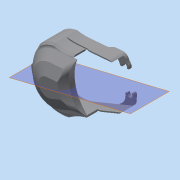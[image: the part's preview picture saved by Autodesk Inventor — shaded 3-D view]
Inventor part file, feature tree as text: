
AUTODESK INVENTOR PART (.ipt)
format: ipt  version: 2015 SP1 (Build 190203100, 203)  size: 975,360 bytes
history: native  units: in
note: dims shown in document units (in); Inventor stores cm internally (conversion verified against a paired STEP export)
features: extrude x14, fillet x14, sketch x14, chamfer x10, projected_geometry x9, other x3, plane x2, mirror x2, direct_edit x1, move_body x1
ambient origin geometry x8: Origin, YZ Plane, XZ Plane, XY Plane, X Axis, Y Axis, Z Axis, Center Point
bodies: Solid2 (feature_tree), Solid1 (feature_tree)
feature tree (70):
  other  "mount_alt.ipt"
  extrude  "Extrusion1"  Depth=0.3937in
  chamfer  "Chamfer1"  Distance=1.0in
  extrude  "Extrusion2"  Depth=1.4173in
  extrude  "Extrusion3"  Depth=0.8268in
  extrude  "Extrusion4"  Depth=2.7559in
  plane  "Work Plane1"
  extrude  "Extrusion5"  Depth=0.0625in TaperAngle=0.0deg
  extrude  "Extrusion6"  Depth=0.375in
  fillet  "Fillet1"  Radius=0.125in
  fillet  "Fillet2"  Radius=0.75in
  fillet  "Fillet3"  Radius=0.75in
  extrude  "Extrusion7"  Depth=0.125in TaperAngle=0.0deg
  extrude  "Extrusion9"  Depth=0.25in
  mirror  "Mirror1"
  extrude  "Extrusion8"  Depth=1.0in TaperAngle=0.0deg
  fillet  "Fillet5"  Radius=0.7874in
  chamfer  "Chamfer2"  Distance=0.2756in Angle=45.0deg
  extrude  "Extrusion10"  Depth=0.125in TaperAngle=45.0deg
  chamfer  "Chamfer3"  Distance=1.0in
  extrude  "Extrusion11"  TaperAngle=0.0deg  [1 undecoded]
  direct_edit  "Direct Edit1"
  extrude  "Extrusion12"  TaperAngle=15.0deg  [1 undecoded]
  chamfer  "Chamfer4"  Angle=15.0deg  [1 undecoded]
  plane  "Work Plane2"
  chamfer  "Chamfer5"  Distance=1.0in
  chamfer  "Chamfer7"  Distance=0.125in Angle=45.0deg
  fillet  "Fillet11"  Radius=0.0591in
  chamfer  "Chamfer8"  Distance=0.25in Angle=45.0deg
  chamfer  "Chamfer9"  Distance=0.25in
  fillet  "Fillet14"  Radius=0.0394in
  fillet  "Fillet15"  Radius=0.0938in
  fillet  "Fillet16"  Radius=0.5in
  extrude  "Extrusion15"  Depth=0.125in
  fillet  "Fillet23"  Radius=0.125in
  fillet  "Fillet24"  Radius=0.0787in
  fillet  "Fillet25"  Radius=0.75in
  mirror  "Mirror3"
  extrude  "Extrusion16"  Depth=1.0in TaperAngle=0.0deg
  chamfer  "Chamfer10"  Distance=0.125in
  fillet  "Fillet26"  Radius=2.0in
  fillet  "Fillet27"  Radius=0.5in
  chamfer  "Chamfer11"  Distance=0.0787in
  fillet  "Fillet28"  Radius=1.0in
  other  "Solid1::mount_alt.ipt"
  other  "TaggingFeature1"
  sketch  "Sketch1"  dims[d0=0.3937in d1=3.3465in d2=1.0in d3=0.0in]
  sketch  "Sketch2"  dims[d4=0.5in d5=0.125in d6=45.0deg d7=1.4173in]
  sketch  "Sketch3"  dims[d8=0.6299in d9=0.0in d10=0.8268in]
  projected_geometry  "Projected Loop1"
  sketch  "Sketch4"  dims[d11=0.315in d12=0.0in d13=2.7559in]
  sketch  "Sketch5"  dims[d14=0.5118in d15=0.0in d16=0.0625in d17=0.0in]
  projected_geometry  "Projected Loop2"
  projected_geometry  "Projected Loop3"
  sketch  "Sketch6"  dims[d18=0.22in d19=0.375in d20=0.125in d21=0.0in d22=0.75in d23=0.75in]
  projected_geometry  "Projected Loop4"
  projected_geometry  "Projected Loop5"
  sketch  "Sketch7"  dims[d24=0.5in d25=0.125in d26=0.0in]
  sketch  "Sketch8"  dims[d27=0.25in d28=0.25in]
  sketch  "Sketch9"  dims[d30=0.125in d31=0.0in d34=1.0in d35=0.0in d37=0.7874in]
  projected_geometry  "Projected Loop6"
  sketch  "Sketch10"  dims[d38=0.0394in]
  projected_geometry  "Projected Loop7"
  sketch  "Sketch11"  dims[d39=0.0197in]
  projected_geometry  "Projected Loop8"
  sketch  "Sketch12"  dims[d40=0.5in d41=0.2756in d42=0.125in d43=45.0deg]
  sketch  "Sketch15"  dims[d44=1.0in d45=0.0in d46=0.125in d47=0.125in d48=45.0deg]
  sketch  "Sketch16"  dims[d49=0.0138in d50=1.0in d51=0.0in d52=0.0in d53=0.0in d54=-0.0079in d55=15.0deg d56=15.0deg d57=1.0in d58=0.0in d59=0.125in d60=0.125in d61=45.0deg d73=0.0591in d74=0.125in d75=45.0deg d82=0.25in d83=0.125in d84=45.0deg d85=0.25in d86=0.0394in d87=0.125in d88=45.0deg d91=0.0938in d92=0.125in d93=45.0deg d94=0.5in d95=0.125in d96=0.125in d98=0.0787in d99=0.75in d100=1.0in d101=0.0in d108=0.125in d109=2.0in d110=0.5in d112=0.0787in d113=1.0in d114=0.0in d115=0.0787in d116=0.125in d117=45.0deg d118=0.5in d119=0.125in d120=0.0787in d121=0.125in d122=45.0deg d123=0.25in]
  projected_geometry  "Projected Loop10"
  move_body  "Move1"
note: 3 required parameter values undecoded (feature->parameter linkage not recoverable at this tier; creation-order binding heuristic only, values carry confidence <= 0.55)
